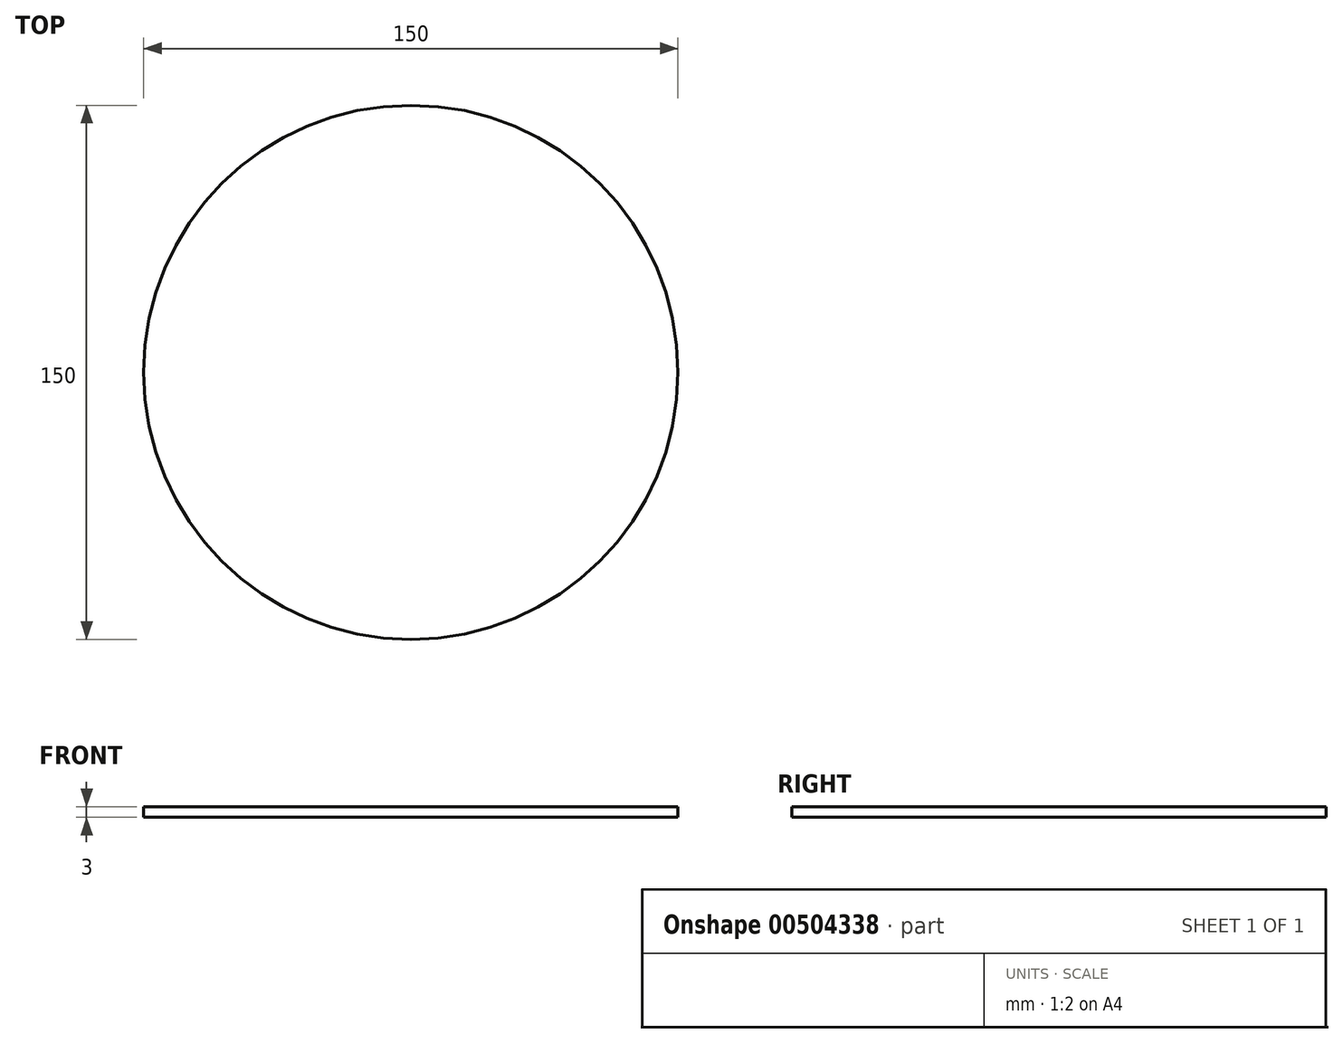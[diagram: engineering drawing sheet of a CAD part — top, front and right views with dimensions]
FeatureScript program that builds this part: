
annotation { "Feature Type Name" : "Feature", "Feature Type Description" : "" }
export const myFeature = defineFeature(function(context is Context, id is Id, definition is map)
    precondition{}
    {
        {
            var Q0;
            Q0=qCreatedBy(makeId("Top.planeOp"),FACE);
            var sketch = newSketch(context, id + "F0", { "sketchPlane" : qUnion([Q0])});
            skLineSegment(sketch, "E0", {"start": v(0, 0) * mm, "end": v(-75, 0) * mm});
            skCircle(sketch, "E1", {"center": v(0, 0) * mm, "radius": 75 * mm});
            skSolve(sketch);
        }
        {
            var Q0;
            Q0 = qSketchRegion(id + "F0", true);
            extrude(context, id + "F1", {"entities" : qUnion([Q0]), "depth" : 3 * mm});
        }
    });
